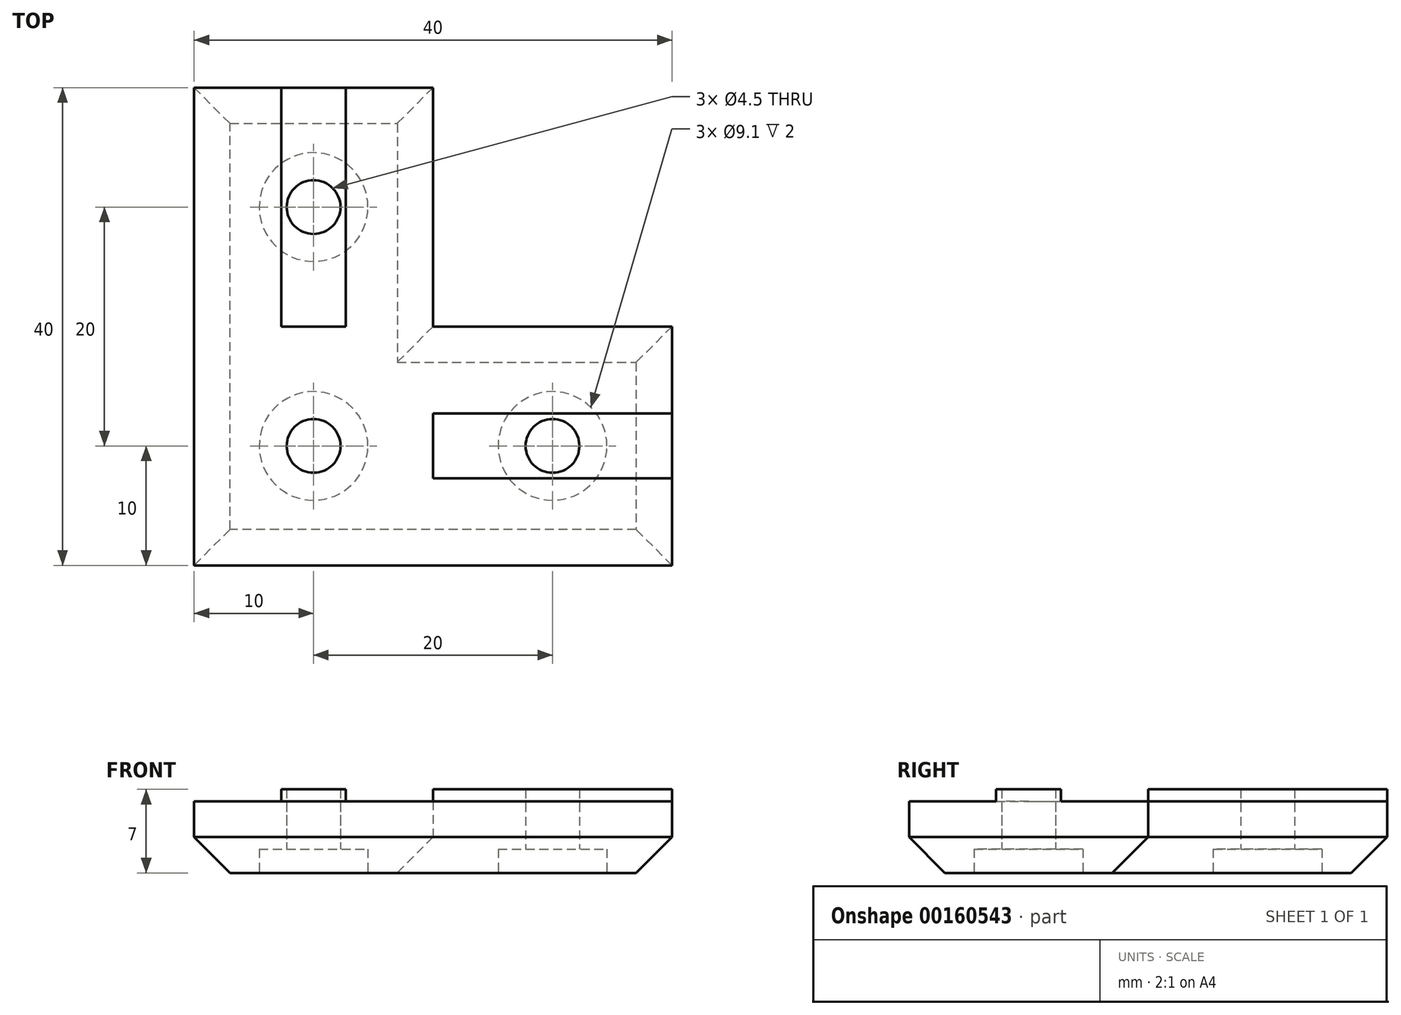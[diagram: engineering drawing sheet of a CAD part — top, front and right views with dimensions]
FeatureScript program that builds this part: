
annotation { "Feature Type Name" : "Feature", "Feature Type Description" : "" }
export const myFeature = defineFeature(function(context is Context, id is Id, definition is map)
    precondition{}
    {
        {
            var Q0;
            Q0=qCreatedBy(makeId("Top.planeOp"),FACE);
            var sketch = newSketch(context, id + "F0", { "sketchPlane" : qUnion([Q0])});
            skLineSegment(sketch, "E0", {"start": v(0, 0) * mm, "end": v(0, 40) * mm});
            skLineSegment(sketch, "E1", {"start": v(0, 40) * mm, "end": v(20, 40) * mm});
            skLineSegment(sketch, "E2", {"start": v(20, 40) * mm, "end": v(20, 20) * mm});
            skLineSegment(sketch, "E3", {"start": v(20, 20) * mm, "end": v(40, 20) * mm});
            skLineSegment(sketch, "E4", {"start": v(40, 20) * mm, "end": v(40, 0) * mm});
            skLineSegment(sketch, "E5", {"start": v(40, 0) * mm, "end": v(0, 0) * mm});
            skSolve(sketch);
        }
        {
            var Q0;
            Q0 = qSketchRegion(id + "F0", true);
            extrude(context, id + "F1", {"entities" : qUnion([Q0]), "depth" : 6 * mm});
        }
        {
            var Q0;
            Q0=makeQuery(id+"F1.opExtrude","CAP_FACE",FACE,{"disambiguationData":[OSD([sQuery(id+"F0.wireOp",EDGE,"E0"),sQuery(id+"F0.wireOp",EDGE,"E1"),sQuery(id+"F0.wireOp",EDGE,"E2"),sQuery(id+"F0.wireOp",EDGE,"E3"),sQuery(id+"F0.wireOp",EDGE,"E4"),sQuery(id+"F0.wireOp",EDGE,"E5")])],"isStart":false});
            var sketch = newSketch(context, id + "F2", { "sketchPlane" : qUnion([Q0])});
            skLineSegment(sketch, "E6", {"start": v(7.3, 40) * mm, "end": v(12.71, 40) * mm});
            skLineSegment(sketch, "E7", {"start": v(12.71, 40) * mm, "end": v(12.71, 20) * mm});
            skLineSegment(sketch, "E8", {"start": v(12.71, 20) * mm, "end": v(10, 20) * mm});
            skPoint(sketch, "E8.endSnap0", {"position": v(10, 40) * mm});
            skLineSegment(sketch, "E9", {"start": v(10, 20) * mm, "end": v(7.3, 20) * mm});
            skLineSegment(sketch, "E10", {"start": v(7.3, 20) * mm, "end": v(7.3, 40) * mm});
            skLineSegment(sketch, "E11", {"start": v(40, 12.71) * mm, "end": v(40, 7.3) * mm});
            skLineSegment(sketch, "E12", {"start": v(40, 7.3) * mm, "end": v(20, 7.3) * mm});
            skLineSegment(sketch, "E13", {"start": v(20, 7.3) * mm, "end": v(20, 10) * mm});
            skPoint(sketch, "E13.endSnap0", {"position": v(40, 10) * mm});
            skLineSegment(sketch, "E14", {"start": v(20, 10) * mm, "end": v(20, 12.71) * mm});
            skLineSegment(sketch, "E15", {"start": v(20, 12.71) * mm, "end": v(40, 12.71) * mm});
            skSolve(sketch);
        }
        {
            var Q0;
            Q0 = qSketchRegion(id + "F2", true);
            extrude(context, id + "F3", {"entities" : qUnion([Q0]), "operationType" : NewBodyOperationType.ADD, "flatOperationType" : FlatOperationType.REMOVE, "offsetDistance" : 25 * mm, "depth" : 1 * mm, "domain" : OperationDomain.MODEL});
        }
        {
            var Q0;
            Q0=makeQuery(id+"F1.opExtrude","CAP_FACE",FACE,{"disambiguationData":[OSD([sQuery(id+"F0.wireOp",EDGE,"E0"),sQuery(id+"F0.wireOp",EDGE,"E1"),sQuery(id+"F0.wireOp",EDGE,"E2"),sQuery(id+"F0.wireOp",EDGE,"E3"),sQuery(id+"F0.wireOp",EDGE,"E4"),sQuery(id+"F0.wireOp",EDGE,"E5")])],"isStart":true});
            var sketch = newSketch(context, id + "F4", { "sketchPlane" : qUnion([Q0])});
            skCircle(sketch, "E16", {"center": v(10, -30) * mm, "radius": 2.25 * mm});
            skCircle(sketch, "E17", {"center": v(10, -10) * mm, "radius": 2.25 * mm});
            skCircle(sketch, "E18", {"center": v(30, -10) * mm, "radius": 2.25 * mm});
            skSolve(sketch);
        }
        {
            var Q0;
            Q0 = qSketchRegion(id + "F4", true);
            extrude(context, id + "F5", {"entities" : qUnion([Q0]), "operationType" : NewBodyOperationType.REMOVE, "endBound" : BoundingType.THROUGH_ALL, "oppositeDirection" : true, "depth" : 25 * mm});
        }
        {
            var Q0;
            Q0=makeQuery(id+"F1.opExtrude","CAP_FACE",FACE,{"disambiguationData":[OSD([sQuery(id+"F0.wireOp",EDGE,"E0"),sQuery(id+"F0.wireOp",EDGE,"E1"),sQuery(id+"F0.wireOp",EDGE,"E2"),sQuery(id+"F0.wireOp",EDGE,"E3"),sQuery(id+"F0.wireOp",EDGE,"E4"),sQuery(id+"F0.wireOp",EDGE,"E5")])],"isStart":true});
            var sketch = newSketch(context, id + "F6", { "sketchPlane" : qUnion([Q0])});
            skCircle(sketch, "E19", {"center": v(10, -10) * mm, "radius": 4.55 * mm});
            skCircle(sketch, "E20", {"center": v(30, -10) * mm, "radius": 4.55 * mm});
            skCircle(sketch, "E21", {"center": v(10, -30) * mm, "radius": 4.55 * mm});
            skSolve(sketch);
        }
        {
            var Q0;
            Q0 = qSketchRegion(id + "F6", true);
            extrude(context, id + "F7", {"entities" : qUnion([Q0]), "operationType" : NewBodyOperationType.REMOVE, "oppositeDirection" : true, "depth" : 2 * mm});
        }
        {
            var Q0;
            Q0=makeQuery(id+"F1.opExtrude","CAP_EDGE",EDGE,{"disambiguationData":[OSD([sQuery(id+"F0.wireOp",EDGE,"E5")])],"isStart":true});
            var Q1;
            Q1=makeQuery(id+"F1.opExtrude","CAP_EDGE",EDGE,{"disambiguationData":[OSD([sQuery(id+"F0.wireOp",EDGE,"E0")])],"isStart":true});
            var Q2;
            Q2=makeQuery(id+"F1.opExtrude","CAP_EDGE",EDGE,{"disambiguationData":[OSD([sQuery(id+"F0.wireOp",EDGE,"E2")])],"isStart":true});
            var Q3;
            Q3=makeQuery(id+"F1.opExtrude","CAP_EDGE",EDGE,{"disambiguationData":[OSD([sQuery(id+"F0.wireOp",EDGE,"E3")])],"isStart":true});
            var Q4;
            Q4=makeQuery(id+"F1.opExtrude","CAP_EDGE",EDGE,{"disambiguationData":[OSD([sQuery(id+"F0.wireOp",EDGE,"E4")])],"isStart":true});
            var Q5;
            Q5=makeQuery(id+"F1.opExtrude","CAP_EDGE",EDGE,{"disambiguationData":[OSD([sQuery(id+"F0.wireOp",EDGE,"E1")])],"isStart":true});
            chamfer(context, id + "F8", {"entities" : qUnion([Q0, Q1, Q2, Q3, Q4, Q5]), "width" : 3 * mm, "tangentPropagation" : true});
        }
    });
